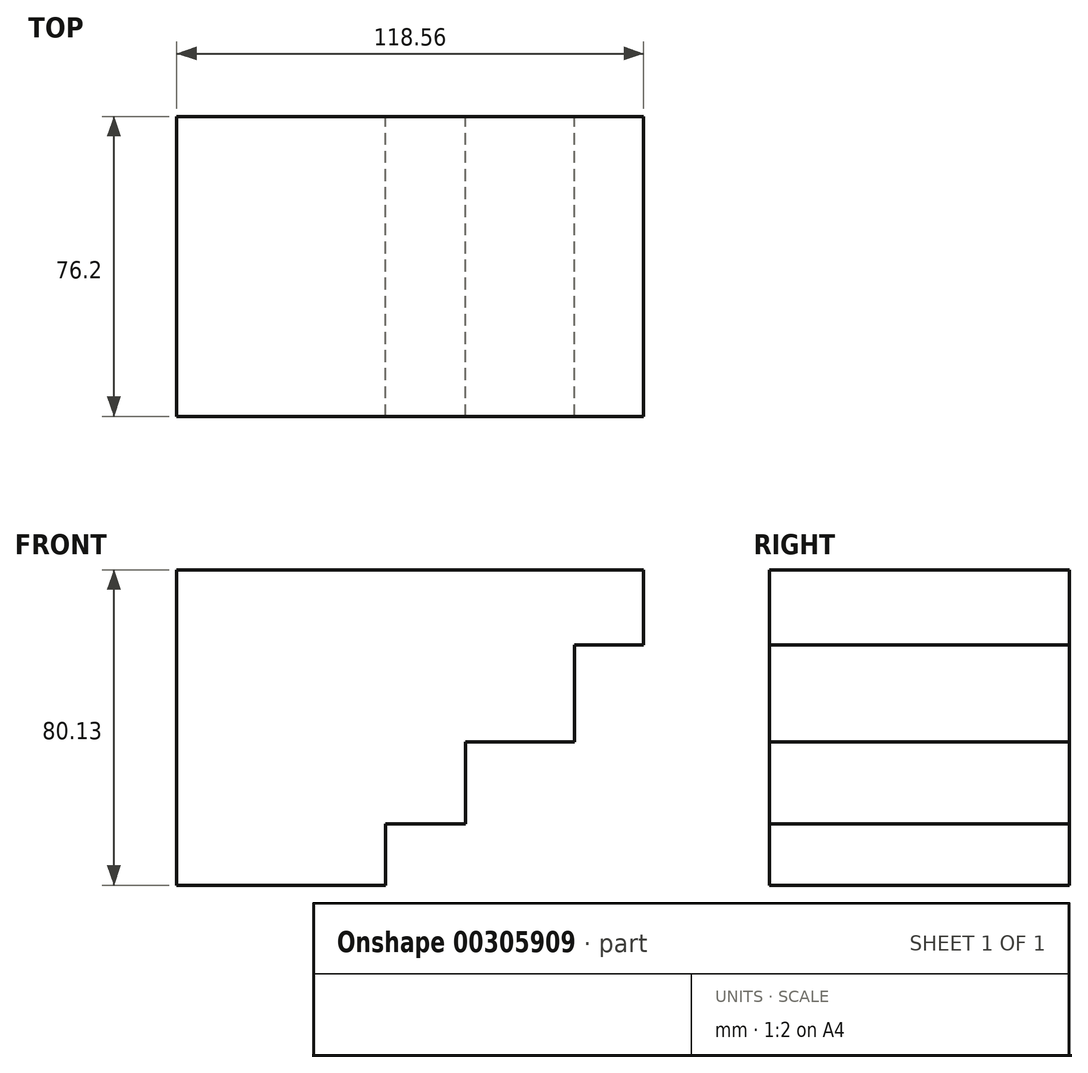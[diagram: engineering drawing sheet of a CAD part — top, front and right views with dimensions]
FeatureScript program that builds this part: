
annotation { "Feature Type Name" : "Feature", "Feature Type Description" : "" }
export const myFeature = defineFeature(function(context is Context, id is Id, definition is map)
    precondition{}
    {
        {
            var Q0;
            Q0=qCreatedBy(makeId("Front.planeOp"),FACE);
            var sketch = newSketch(context, id + "F0", { "sketchPlane" : qUnion([Q0])});
            skLineSegment(sketch, "E0", {"start": v(-53, -61.03) * mm, "end": v(0, -61.03) * mm});
            skLineSegment(sketch, "E1", {"start": v(0, -61.03) * mm, "end": v(0, -45.42) * mm});
            skLineSegment(sketch, "E2", {"start": v(0, -45.42) * mm, "end": v(20.38, -45.42) * mm});
            skLineSegment(sketch, "E3", {"start": v(20.38, -45.42) * mm, "end": v(20.38, -24.7) * mm});
            skLineSegment(sketch, "E4", {"start": v(20.38, -24.7) * mm, "end": v(48.1, -24.7) * mm});
            skLineSegment(sketch, "E5", {"start": v(48.1, -24.7) * mm, "end": v(48.1, 0) * mm});
            skLineSegment(sketch, "E6", {"start": v(48.1, 0) * mm, "end": v(65.57, 0) * mm});
            skLineSegment(sketch, "E7", {"start": v(65.57, 0) * mm, "end": v(65.57, 19.1) * mm});
            skLineSegment(sketch, "E8", {"start": v(65.57, 19.1) * mm, "end": v(-53, 19.1) * mm});
            skLineSegment(sketch, "E9", {"start": v(-53, 19.1) * mm, "end": v(-53, -61.03) * mm});
            skSolve(sketch);
        }
        {
            var Q0;
            Q0=makeQuery(id+"F0.imprint","IMPRINT",FACE,{"disambiguationData":[TD([[makeQuery(id+"F0.imprint","IMPRINT",EDGE,{"derivedFrom":sQuery(id+"F0.wireOp",EDGE,"E0")}),1.0]])]});
            extrude(context, id + "F1", {"entities" : qUnion([Q0]), "depth" : 76.2 * mm, "offsetDistance" : 25.4 * mm});
        }
    });
